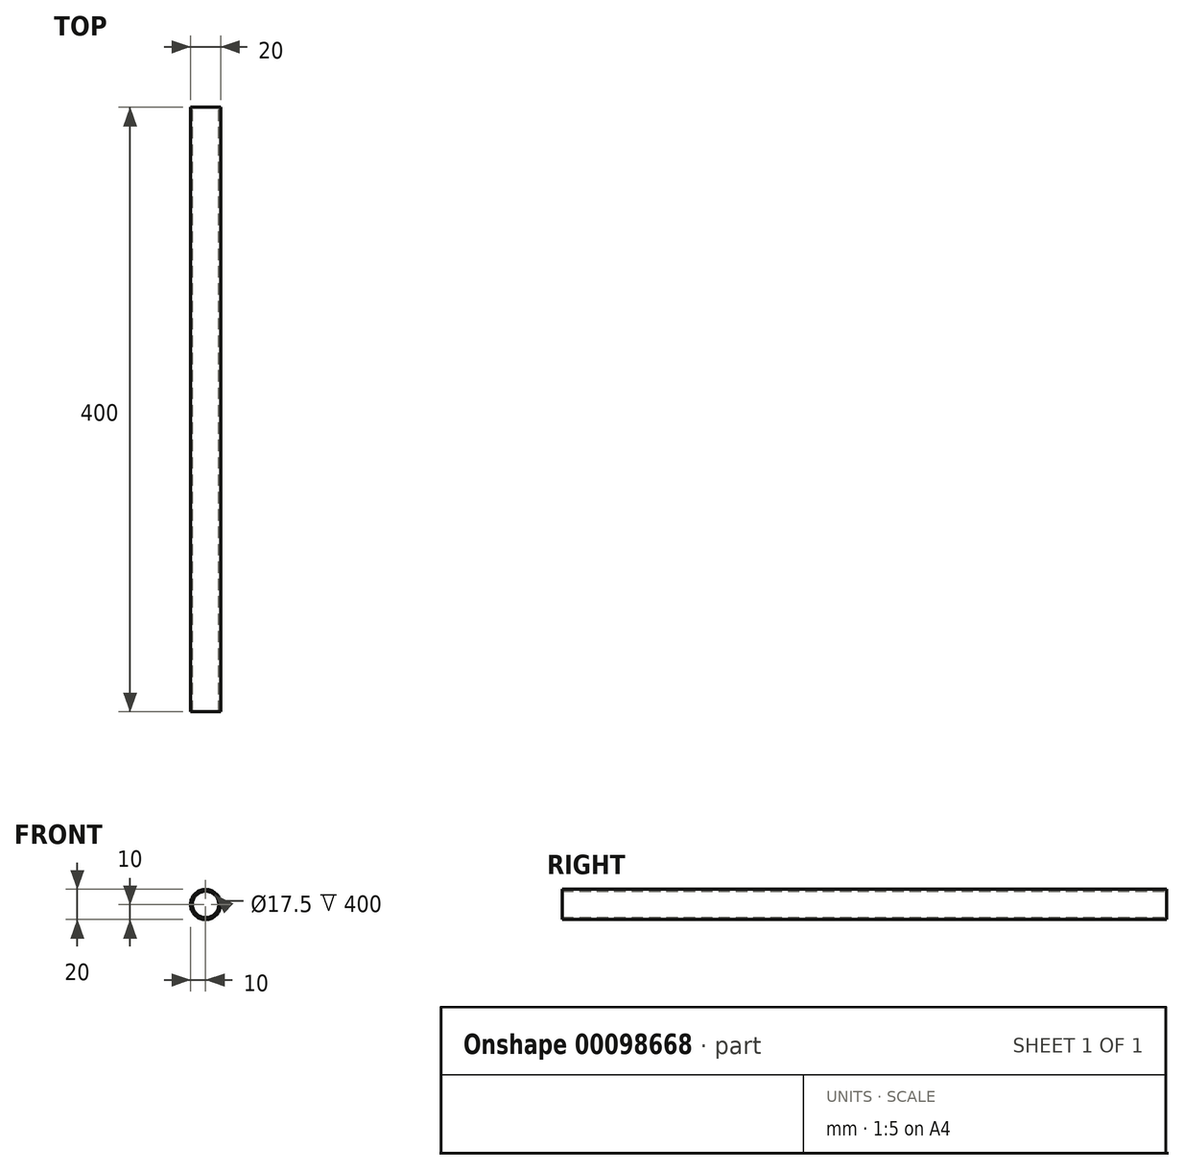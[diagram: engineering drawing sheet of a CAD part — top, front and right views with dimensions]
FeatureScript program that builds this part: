
annotation { "Feature Type Name" : "Feature", "Feature Type Description" : "" }
export const myFeature = defineFeature(function(context is Context, id is Id, definition is map)
    precondition{}
    {
        {
            var Q0;
            Q0=qCreatedBy(makeId("Front.planeOp"),FACE);
            var sketch = newSketch(context, id + "F0", { "sketchPlane" : qUnion([Q0])});
            skCircle(sketch, "E0", {"center": v(0, 0) * mm, "radius": 10 * mm});
            skCircle(sketch, "E1", {"center": v(0, 0) * mm, "radius": 8.75 * mm});
            skSolve(sketch);
        }
        {
            var Q0;
            Q0=qSketchRegion(id+"F0",true);
            extrude(context, id + "F1", {"entities" : qUnion([Q0]), "depth" : 400 * mm});
        }
    });
